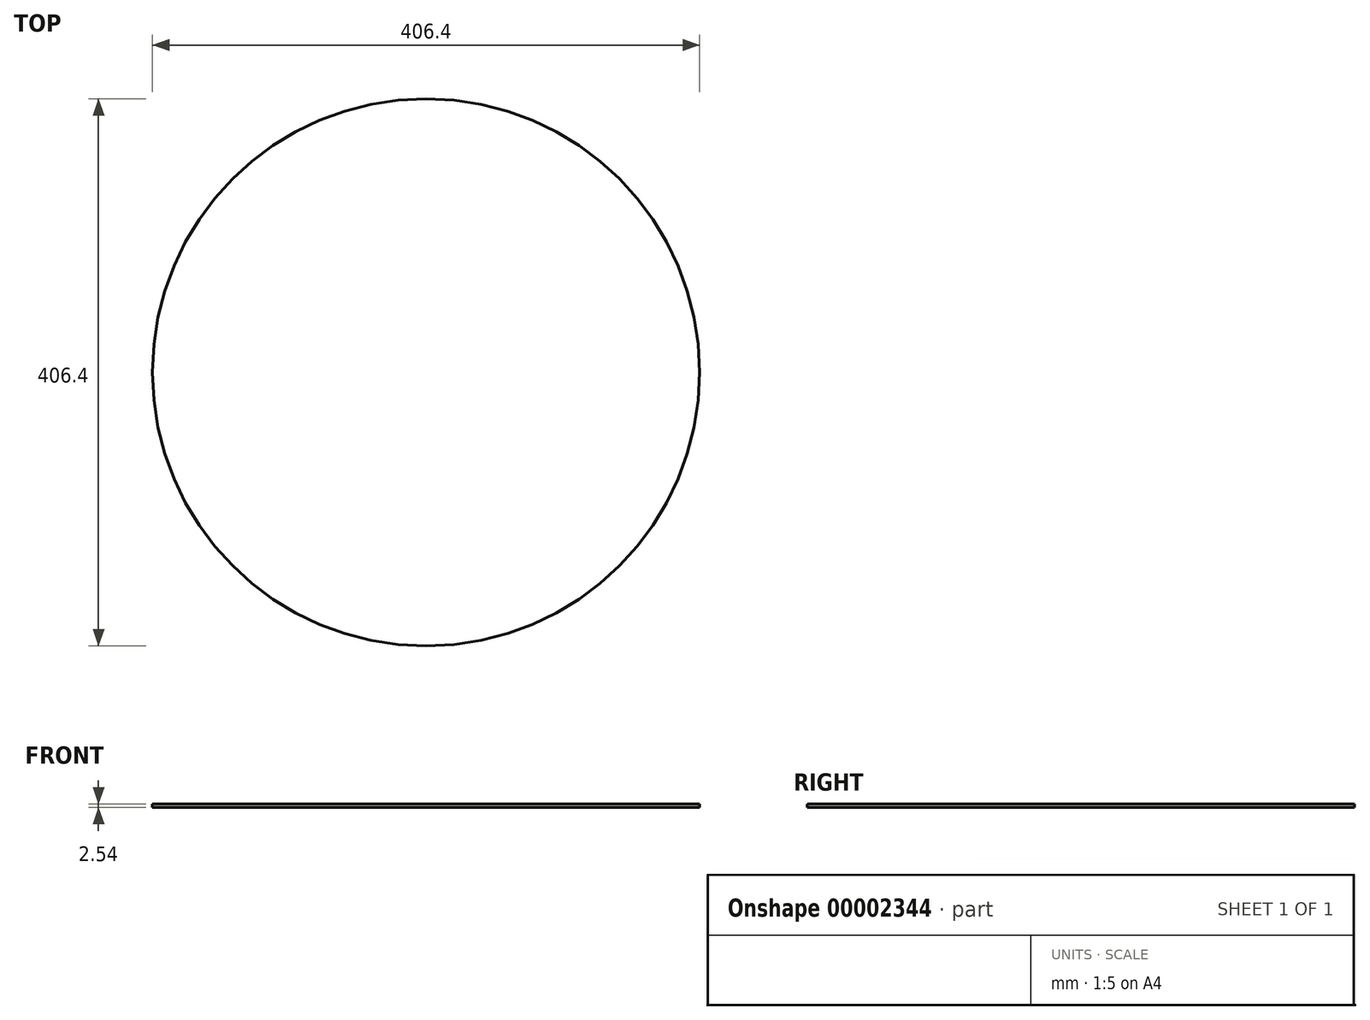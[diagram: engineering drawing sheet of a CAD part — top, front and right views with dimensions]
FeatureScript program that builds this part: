
annotation { "Feature Type Name" : "Feature", "Feature Type Description" : "" }
export const myFeature = defineFeature(function(context is Context, id is Id, definition is map)
    precondition{}
    {
        {
            var Q0;
            Q0=qCreatedBy(makeId("Top.planeOp"),FACE);
            var sketch = newSketch(context, id + "F0", { "sketchPlane" : qUnion([Q0])});
            skCircle(sketch, "E0", {"center": v(0, 0) * mm, "radius": 203.2 * mm});
            skSolve(sketch);
        }
        {
            var Q0;
            Q0=makeQuery(id+"F0.imprint","IMPRINT",FACE,{"disambiguationData":[TD([[makeQuery(id+"F0.imprint","IMPRINT",EDGE,{"derivedFrom":sQuery(id+"F0.wireOp",EDGE,"E0")}),1.0]])]});
            extrude(context, id + "F1", {"entities" : qUnion([Q0]), "depth" : 2.54 * mm});
        }
    });
